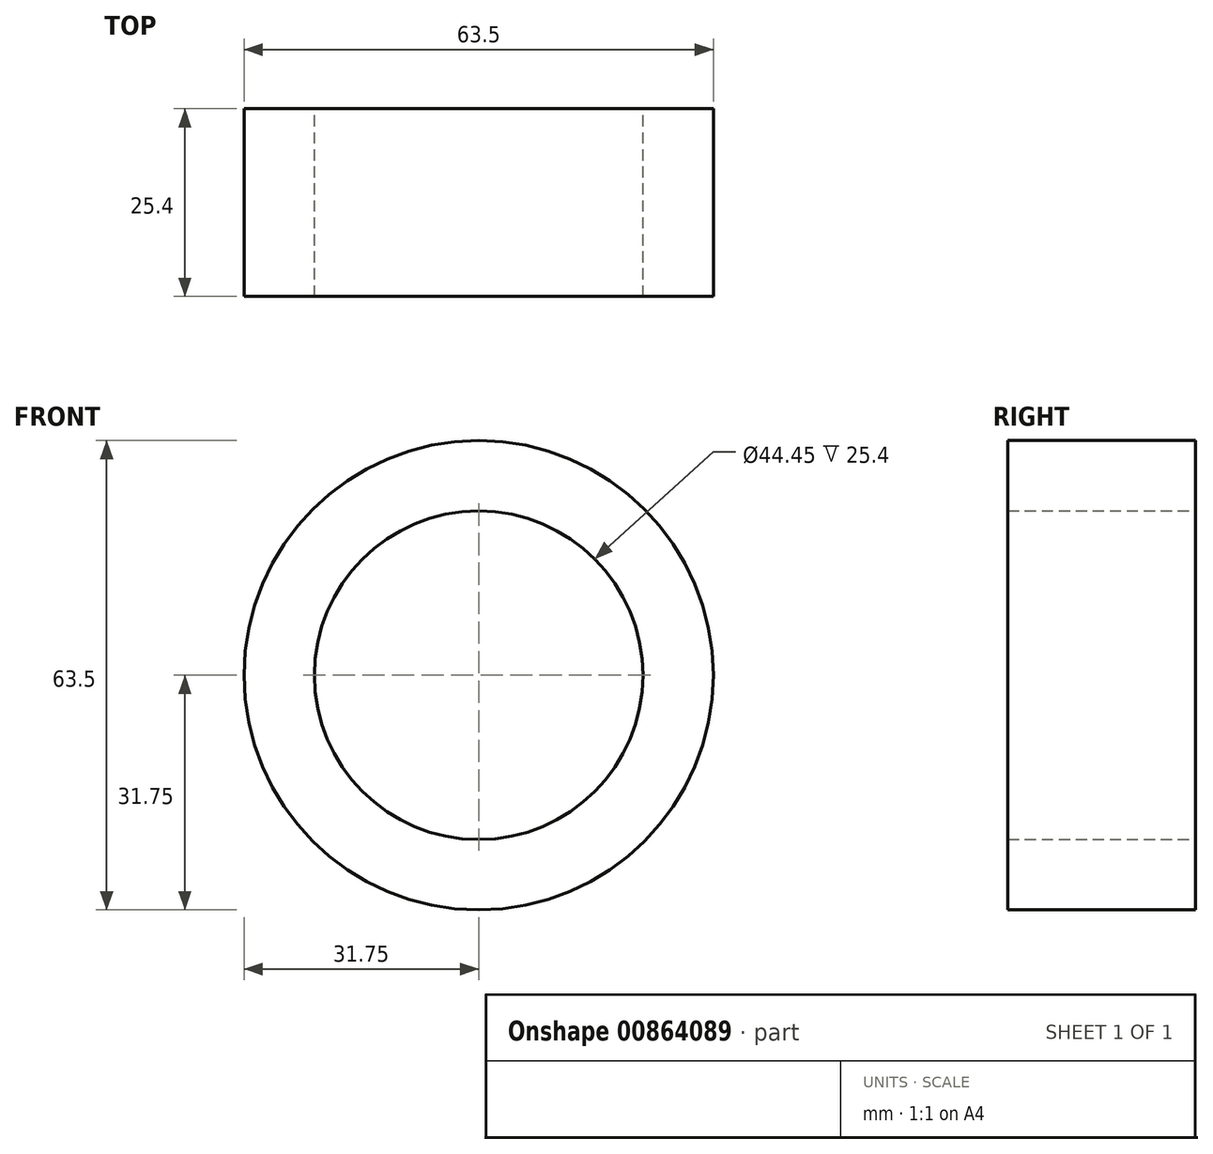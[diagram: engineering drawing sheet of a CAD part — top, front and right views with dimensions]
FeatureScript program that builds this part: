
annotation { "Feature Type Name" : "Feature", "Feature Type Description" : "" }
export const myFeature = defineFeature(function(context is Context, id is Id, definition is map)
    precondition{}
    {
        {
            var Q0;
            Q0=qCreatedBy(makeId("Front.planeOp"),FACE);
            var sketch = newSketch(context, id + "F0", { "sketchPlane" : qUnion([Q0])});
            skCircle(sketch, "E0", {"center": v(0, 0) * mm, "radius": 31.75 * mm});
            skCircle(sketch, "E1", {"center": v(0, 0) * mm, "radius": 22.23 * mm});
            skSolve(sketch);
        }
        {
            var Q0;
            Q0=makeQuery(id+"F0.imprint","IMPRINT",FACE,{"disambiguationData":[TD([[makeQuery(id+"F0.imprint","IMPRINT",EDGE,{"derivedFrom":sQuery(id+"F0.wireOp",EDGE,"E0")}),1.0]])]});
            extrude(context, id + "F1", {"entities" : qUnion([Q0]), "depth" : 25.4 * mm, "offsetDistance" : 25.4 * mm});
        }
    });
